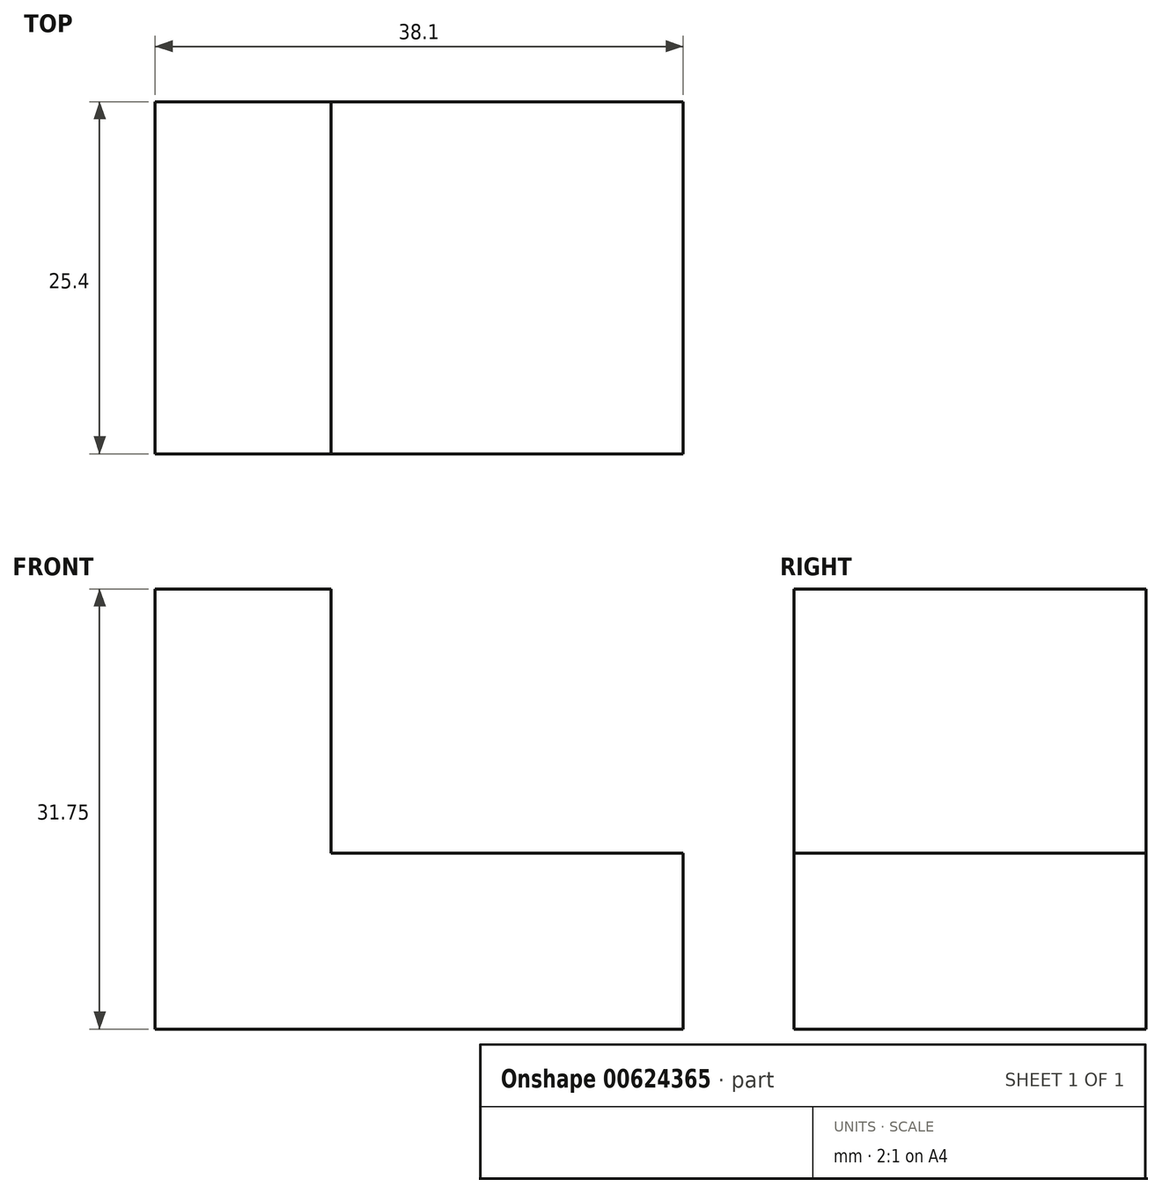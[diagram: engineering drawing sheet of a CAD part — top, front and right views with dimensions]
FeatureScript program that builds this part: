
annotation { "Feature Type Name" : "Feature", "Feature Type Description" : "" }
export const myFeature = defineFeature(function(context is Context, id is Id, definition is map)
    precondition{}
    {
        {
            var Q0;
            Q0=qCreatedBy(makeId("Front.planeOp"),FACE);
            var sketch = newSketch(context, id + "F0", { "sketchPlane" : qUnion([Q0])});
            skLineSegment(sketch, "E0", {"start": v(0, 31.75) * mm, "end": v(0, 0) * mm});
            skLineSegment(sketch, "E1", {"start": v(0, 0) * mm, "end": v(38.1, 0) * mm});
            skLineSegment(sketch, "E2", {"start": v(38.1, 0) * mm, "end": v(38.1, 12.7) * mm});
            skLineSegment(sketch, "E3", {"start": v(38.1, 12.7) * mm, "end": v(12.7, 12.7) * mm});
            skLineSegment(sketch, "E4", {"start": v(12.7, 12.7) * mm, "end": v(12.7, 31.75) * mm});
            skLineSegment(sketch, "E5", {"start": v(12.7, 31.75) * mm, "end": v(0, 31.75) * mm});
            skSolve(sketch);
        }
        {
            var Q0;
            Q0=makeQuery(id+"F0.imprint","IMPRINT",FACE,{"disambiguationData":[TD([[makeQuery(id+"F0.imprint","IMPRINT",EDGE,{"derivedFrom":sQuery(id+"F0.wireOp",EDGE,"E0")}),1.0]])]});
            extrude(context, id + "F1", {"entities" : qUnion([Q0]), "oppositeDirection" : true, "depth" : 25.4 * mm, "offsetDistance" : 25.4 * mm});
        }
    });
